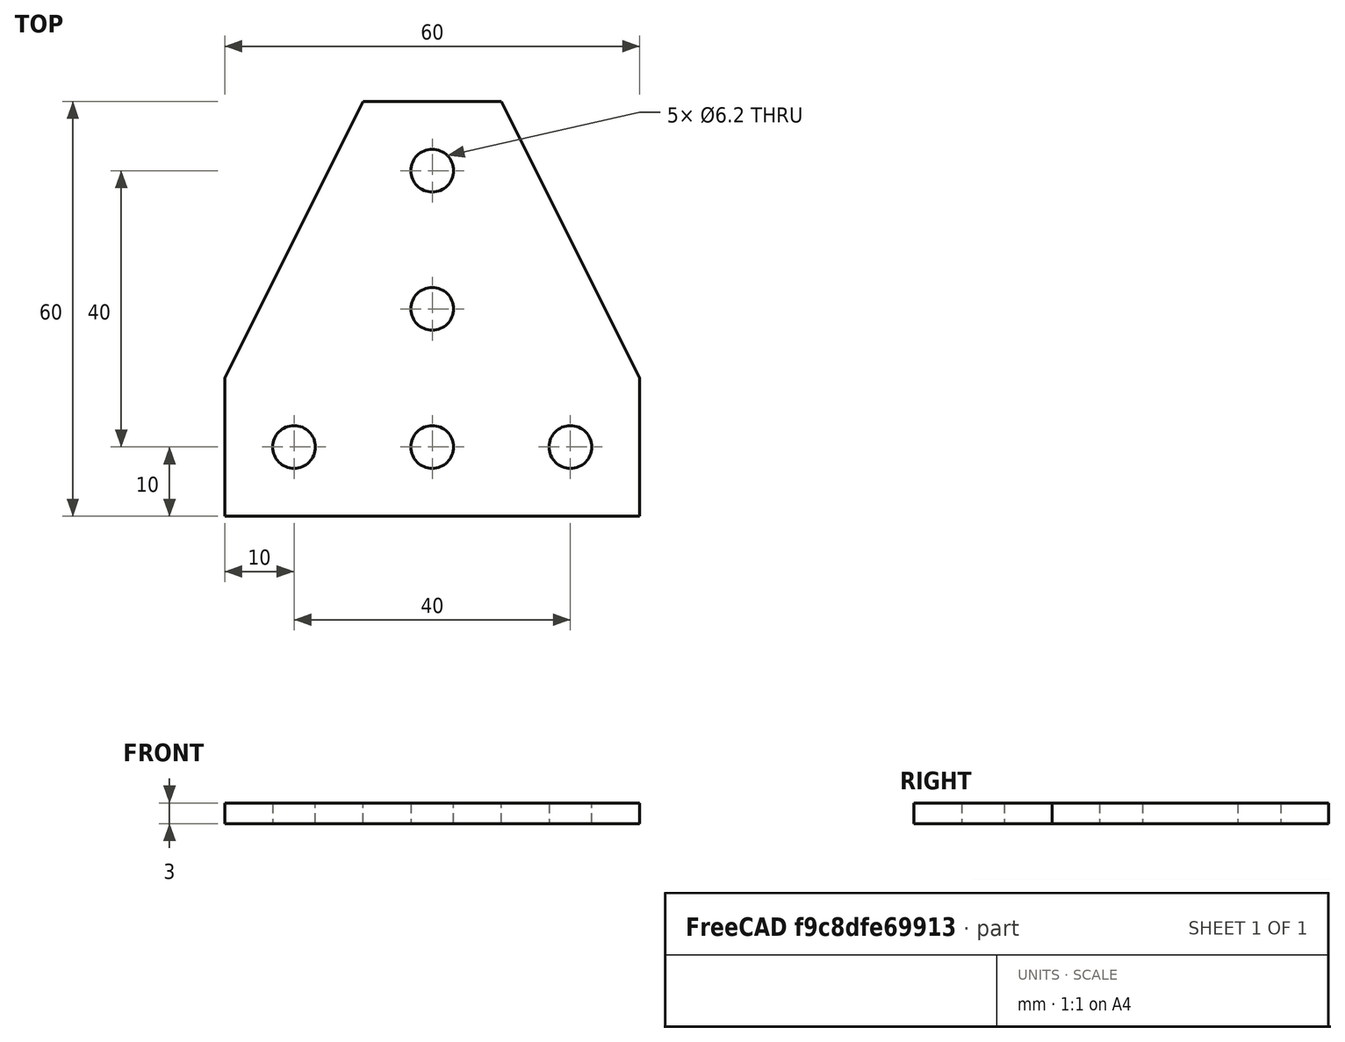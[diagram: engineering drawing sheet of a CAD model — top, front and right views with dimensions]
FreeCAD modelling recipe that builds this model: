
FCSTD DOCUMENT  (FreeCAD 0.19R23964 (Git))
Label: tcon
License: All rights reserved
LicenseURL: http://en.wikipedia.org/wiki/All_rights_reserved
objects: TechDraw::DrawViewDimension×10, TechDraw::DrawViewPart×2, Sketcher::SketchObject×1, PartDesign::Pad×1, PartDesign::Body×1, TechDraw::DrawSVGTemplate×1, TechDraw::DrawViewAnnotation×1, TechDraw::DrawPage×1
note: 4 computed .brp shape members not serialized (recipe doc carries the construction recipe); baked Part::Feature solids carry a one-line shape summary decoded from their .brp

FEATURE [Sketcher::SketchObject] Sketch
  FullyConstrained = false
  MapMode = 5
  Support = -> [XY_Plane]
  sketch-geometry (11):
    g0: LineSegment StartX=0 StartY=0 StartZ=0 EndX=60 EndY=0 EndZ=0
    g1: LineSegment StartX=60 StartY=0 StartZ=0 EndX=60 EndY=20 EndZ=0
    g2: LineSegment StartX=60 StartY=20 StartZ=0 EndX=40 EndY=60 EndZ=0
    g3: LineSegment StartX=40 StartY=60 StartZ=0 EndX=20 EndY=60 EndZ=0
    g4: LineSegment StartX=20 StartY=60 StartZ=0 EndX=0 EndY=20 EndZ=0
    g5: LineSegment StartX=0 StartY=20 StartZ=0 EndX=0 EndY=0 EndZ=0
    g6: Circle CenterX=10 CenterY=10 CenterZ=0 NormalX=0 NormalY=0 NormalZ=1 AngleXU=0 Radius=3.1
    g7: Circle CenterX=30 CenterY=10 CenterZ=0 NormalX=0 NormalY=0 NormalZ=1 AngleXU=0 Radius=3.1
    g8: Circle CenterX=50 CenterY=10 CenterZ=0 NormalX=0 NormalY=0 NormalZ=1 AngleXU=0 Radius=3.1
    g9: Circle CenterX=30 CenterY=30 CenterZ=0 NormalX=0 NormalY=0 NormalZ=1 AngleXU=0 Radius=3.1
    g10: Circle CenterX=30 CenterY=50 CenterZ=0 NormalX=0 NormalY=0 NormalZ=1 AngleXU=0 Radius=3.1
  constraints (32):
    c: Coincident(g0,g1)
    c: Coincident(g1,g2)
    c: Coincident(g2,g3)
    c: Coincident(g3,g4)
    c: Coincident(g4,g5)
    c: Coincident(g5,g0)
    c: Horizontal(g0)
    c: Vertical(g5)
    c: Vertical(g1)
    c: Horizontal(g3)
    c: Coincident(g0,g-1)
    c: DistanceX(g0,g0) = 60
    c: DistanceY(g5,g5) = 20
    c: DistanceY(g0,g1) = 20
    c: DistanceY(g-1,g3) = 60
    c: DistanceX(g-1,g3) = 20
    c: DistanceX(g3,g2) = 20
    c: Radius(g6) = 3.1
    c: DistanceY(g-1,g6) = 10
    c: DistanceX(g-1,g6) = 10
    c: DistanceY(g6,g7) = 0
    c: DistanceY(g7,g8) = 0
    c: DistanceX(g6,g7) = 20
    c: DistanceX(g7,g8) = 20
    c: DistanceX(g9,g7) = 0
    c: DistanceX(g10,g9) = 0
    c: DistanceY(g9,g10) = 20
    c: DistanceY(g7,g9) = 20
    c: Radius(g10) = 3.1
    c: Radius(g9) = 3.1
    c: Radius(g7) = 3.1
    c: Radius(g8) = 3.1
FEATURE [PartDesign::Pad] Pad
  AllowMultiFace = false
  Direction = (1,1,1)
  Length = 3
  Length2 = 100
  Profile = -> Sketch
  Refine = true
  Type = 0
FEATURE [PartDesign::Body] Body
  Group = -> [Sketch,Pad]
  Origin = -> BodyOrigin
  Tip = -> Pad
FEATURE [TechDraw::DrawSVGTemplate] Template
  EditableTexts =  =Links two Profiles;   =One at the end, on in the middle; Approved By=Oliver Schlüter; Classification=CLASSIFICATION; Created By=Lukas Schattenhofer; Date Of Issue=11-07-2021; Document Status=checked; Document Type=Technical Drawing; Identification Number=IDENTIFICATION NUMBER; Legal Owner=OSE Germany; Project name=UniProKitLib; Rev=REV; Scale=1:1; Seg=0/0; Technical Reference=TECHNICAL REFERENCE; Title/Supplementary Title=TCon Verbinder
  Height = 210
  Orientation = 1
  Width = 297
FEATURE [TechDraw::DrawViewPart] View
  CoarseView = false
  Direction = (0,0,1)
  Focus = 100
  HardHidden = false
  IsoCount = 0
  IsoHidden = false
  IsoVisible = false
  LockPosition = false
  Perspective = false
  Rotation = 0
  ScaleType = 0
  SeamHidden = false
  SeamVisible = true
  SmoothHidden = false
  SmoothVisible = true
  Source = -> [Pad]
  X = 89.6167
  XDirection = (1,0,0)
  Y = 148.267
FEATURE [TechDraw::DrawViewDimension] Dimension
  Arbitrary = false
  ArbitraryTolerances = false
  EqualTolerance = true
  FormatSpec = %.2f
  FormatSpecOverTolerance = %+.2f
  FormatSpecUnderTolerance = %+.2f
  Inverted = false
  LockPosition = false
  MeasureType = 1
  OverTolerance = 0
  References2D = -> [View]
  Rotation = 0
  ScaleType = 0
  TheoreticalExact = false
  Type = 1
  UnderTolerance = 0
  X = -0.294149
  Y = -45.6725
FEATURE [TechDraw::DrawViewDimension] Dimension001
  Arbitrary = false
  ArbitraryTolerances = false
  EqualTolerance = true
  FormatSpec = %.2f
  FormatSpecOverTolerance = %+.2f
  FormatSpecUnderTolerance = %+.2f
  Inverted = false
  LockPosition = false
  MeasureType = 1
  OverTolerance = 0
  References2D = -> [View]
  Rotation = 0
  ScaleType = 0
  TheoreticalExact = false
  Type = 1
  UnderTolerance = 0
  X = 0.089983
  Y = -53.7185
FEATURE [TechDraw::DrawViewDimension] Dimension002
  Arbitrary = false
  ArbitraryTolerances = false
  EqualTolerance = true
  FormatSpec = %.2f
  FormatSpecOverTolerance = %+.2f
  FormatSpecUnderTolerance = %+.2f
  Inverted = false
  LockPosition = false
  MeasureType = 1
  OverTolerance = 0
  References2D = -> [View]
  Rotation = 0
  ScaleType = 0
  TheoreticalExact = false
  Type = 2
  UnderTolerance = 0
  X = -36.8551
  Y = -22.2822
FEATURE [TechDraw::DrawViewDimension] Dimension003
  Arbitrary = false
  ArbitraryTolerances = false
  EqualTolerance = true
  FormatSpec = %.2f
  FormatSpecOverTolerance = %+.2f
  FormatSpecUnderTolerance = %+.2f
  Inverted = false
  LockPosition = false
  MeasureType = 1
  OverTolerance = 0
  References2D = -> [View]
  Rotation = 0
  ScaleType = 0
  TheoreticalExact = false
  Type = 2
  UnderTolerance = 0
  X = -54.3062
  Y = -11.9961
FEATURE [TechDraw::DrawViewDimension] Dimension004
  Arbitrary = false
  ArbitraryTolerances = false
  EqualTolerance = true
  FormatSpec = %.2f
  FormatSpecOverTolerance = %+.2f
  FormatSpecUnderTolerance = %+.2f
  Inverted = false
  LockPosition = false
  MeasureType = 1
  OverTolerance = 0
  References2D = -> [View]
  Rotation = 0
  ScaleType = 0
  TheoreticalExact = false
  Type = 2
  UnderTolerance = 0
  X = -62.6025
  Y = -2.71134
FEATURE [TechDraw::DrawViewDimension] Dimension005
  Arbitrary = false
  ArbitraryTolerances = false
  EqualTolerance = true
  FormatSpec = %.2f
  FormatSpecOverTolerance = %+.2f
  FormatSpecUnderTolerance = %+.2f
  Inverted = false
  LockPosition = false
  MeasureType = 1
  OverTolerance = 0
  References2D = -> [View]
  Rotation = 0
  ScaleType = 0
  TheoreticalExact = false
  Type = 2
  UnderTolerance = 0
  X = -70.9355
  Y = -2.71778
FEATURE [TechDraw::DrawViewDimension] Dimension006
  Arbitrary = false
  ArbitraryTolerances = false
  EqualTolerance = true
  FormatSpec = %.2f
  FormatSpecOverTolerance = %+.2f
  FormatSpecUnderTolerance = %+.2f
  Inverted = false
  LockPosition = false
  MeasureType = 1
  OverTolerance = 0
  References2D = -> [View]
  Rotation = 0
  ScaleType = 0
  TheoreticalExact = false
  Type = 2
  UnderTolerance = 0
  X = -45.7426
  Y = -16.89
FEATURE [TechDraw::DrawViewDimension] Dimension007
  Arbitrary = false
  ArbitraryTolerances = false
  EqualTolerance = true
  FormatSpec = %.2f
  FormatSpecOverTolerance = %+.2f
  FormatSpecUnderTolerance = %+.2f
  Inverted = false
  LockPosition = false
  MeasureType = 1
  OverTolerance = 0
  References2D = -> [View]
  Rotation = 0
  ScaleType = 0
  TheoreticalExact = false
  Type = 1
  UnderTolerance = 0
  X = 0
  Y = -36.5635
FEATURE [TechDraw::DrawViewDimension] Dimension008
  Arbitrary = false
  ArbitraryTolerances = false
  EqualTolerance = true
  FormatSpec = R%.2f
  FormatSpecOverTolerance = %+.2f
  FormatSpecUnderTolerance = %+.2f
  Inverted = false
  LockPosition = false
  MeasureType = 1
  OverTolerance = 0
  References2D = -> [View]
  Rotation = 0
  ScaleType = 0
  TheoreticalExact = false
  Type = 4
  UnderTolerance = 0
  X = 30.2732
  Y = 43.0594
FEATURE [TechDraw::DrawViewAnnotation] Annotation
  Font = osifont
  LineSpace = 80
  LockPosition = false
  MaxWidth = -1
  Rotation = 0
  ScaleType = 0
  Text = All wholes have a radius of R3,10mm. | Material: Aluminium, ABS, PLA (depending on desired strenght
  TextSize = 5
  TextStyle = 0
  X = 217.948
  Y = 88.1839
FEATURE [TechDraw::DrawViewPart] View001
  CoarseView = false
  Direction = (-1,0,0)
  Focus = 100
  HardHidden = false
  IsoCount = 0
  IsoHidden = false
  IsoVisible = false
  LockPosition = false
  Perspective = false
  Rotation = 0
  ScaleType = 0
  SeamHidden = false
  SeamVisible = true
  SmoothHidden = false
  SmoothVisible = true
  Source = -> [Pad]
  X = 174.819
  XDirection = (0,0,1)
  Y = 147.889
FEATURE [TechDraw::DrawViewDimension] Dimension009
  Arbitrary = false
  ArbitraryTolerances = false
  EqualTolerance = true
  FormatSpec = %.2f
  FormatSpecOverTolerance = %+.2f
  FormatSpecUnderTolerance = %+.2f
  Inverted = false
  LockPosition = false
  MeasureType = 1
  OverTolerance = 0
  References2D = -> [View001]
  Rotation = 0
  ScaleType = 0
  TheoreticalExact = false
  Type = 1
  UnderTolerance = 0
  X = -0.741525
  Y = 41.8644
FEATURE [TechDraw::DrawPage] Page  label="Technical Drawing"
  KeepUpdated = true
  NextBalloonIndex = 1
  ProjectionType = 0
  Template = -> Template
  Views = -> [View,Dimension,Dimension001,Dimension002,Dimension003,Dimension004,Dimension005,Dimension006,Dimension007,Dimension008,Annotation,View001,Dimension009]
